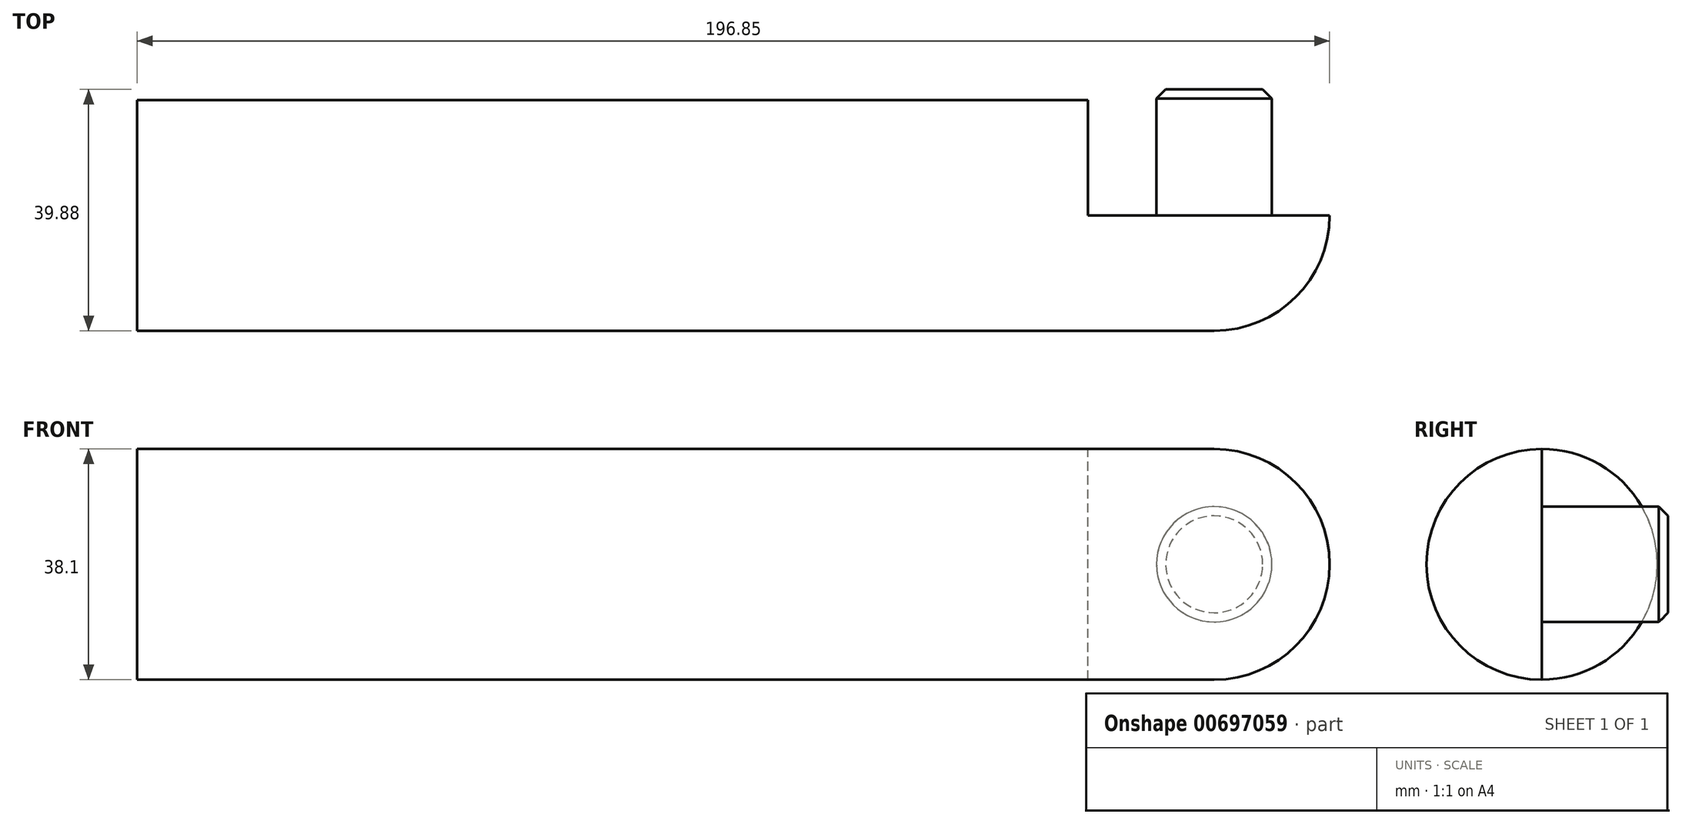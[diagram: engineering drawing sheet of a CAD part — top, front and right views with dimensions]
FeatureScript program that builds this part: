
annotation { "Feature Type Name" : "Feature", "Feature Type Description" : "" }
export const myFeature = defineFeature(function(context is Context, id is Id, definition is map)
    precondition{}
    {
        {
            var Q0;
            Q0=qCreatedBy(makeId("Front.planeOp"),FACE);
            var sketch = newSketch(context, id + "F0", { "sketchPlane" : qUnion([Q0])});
            skLineSegment(sketch, "E0.bottom", {"start": v(78.49, 19.05) * mm, "end": v(-78.49, 19.05) * mm});
            skLineSegment(sketch, "E0.top", {"start": v(78.49, -19.05) * mm, "end": v(-78.49, -19.05) * mm});
            skLineSegment(sketch, "E0.left", {"start": v(78.49, 19.05) * mm, "end": v(78.49, -19.05) * mm});
            skLineSegment(sketch, "E0.right", {"start": v(-78.49, 19.05) * mm, "end": v(-78.49, -19.05) * mm});
            skPoint(sketch, "E0.middle", {"position": v(0, 0) * mm});
            skLineSegment(sketch, "E1", {"start": v(78.49, 0) * mm, "end": v(-78.49, 0) * mm});
            skSolve(sketch);
        }
        {
            var Q0;
            Q0=qCreatedBy(makeId("Front.planeOp"),FACE);
            var sketch = newSketch(context, id + "F1", { "sketchPlane" : qUnion([Q0])});
            skLineSegment(sketch, "E2", {"start": v(78.49, 19.05) * mm, "end": v(99.31, 19.05) * mm});
            skLineSegment(sketch, "E3", {"start": v(78.49, -19.05) * mm, "end": v(99.31, -19.05) * mm});
            skLineSegment(sketch, "E4", {"start": v(99.31, 19.05) * mm, "end": v(99.31, -19.05) * mm});
            skLineSegment(sketch, "E5", {"start": v(78.49, 0) * mm, "end": v(99.31, 0) * mm});
            skLineSegment(sketch, "E6.0", {"start": v(78.49, 19.05) * mm, "end": v(78.49, -19.05) * mm});
            skSolve(sketch);
        }
        {
            var Q0;
            {var subQ0=sQuery(id+"F0.wireOp",EDGE,"E0.bottom");Q0=makeQuery(id+"F0.imprint","IMPRINT",FACE,{"disambiguationData":[TD([[makeQuery(id+"F0.imprint","IMPRINT",EDGE,{"derivedFrom":subQ0}),1.0]])]});}
            var Q1;
            Q1=sQuery(id+"F0.wireOp",EDGE,"E1");
            revolve(context, id + "F2", {"entities" : qUnion([Q0]), "axis" : qUnion([Q1]), "revolveType" : RevolveType.FULL});
        }
        {
            var Q0;
            {var subQ0=sQuery(id+"F1.wireOp",EDGE,"E2");Q0=makeQuery(id+"F1.imprint","IMPRINT",FACE,{"disambiguationData":[TD([[makeQuery(id+"F1.imprint","IMPRINT",EDGE,{"derivedFrom":subQ0}),-1.0]])]});}
            var Q1;
            Q1=sQuery(id+"F1.wireOp",EDGE,"E5");
            revolve(context, id + "F3", {"operationType" : NewBodyOperationType.ADD, "entities" : qUnion([Q0]), "axis" : qUnion([Q1]), "revolveType" : RevolveType.ONE_DIRECTION, "angle" : 180 * degree});
        }
        {
            var Q0;
            Q0=makeQuery(id+"F3.opRevolve","SWEPT_FACE",FACE,{"disambiguationData":[OSD([sQuery(id+"F1.wireOp",EDGE,"E4")])]});
            var Q1;
            Q1=sQuery(id+"F1.wireOp",EDGE,"E4");
            revolve(context, id + "F4", {"operationType" : NewBodyOperationType.ADD, "entities" : qUnion([Q0]), "axis" : qUnion([Q1]), "revolveType" : RevolveType.ONE_DIRECTION, "oppositeDirection" : true, "angle" : 90 * degree});
        }
        {
            var Q0;
            Q0=qCreatedBy(makeId("Front.planeOp"),FACE);
            var sketch = newSketch(context, id + "F5", { "sketchPlane" : qUnion([Q0])});
            skCircle(sketch, "E7", {"center": v(99.31, 0) * mm, "radius": 9.53 * mm});
            skSolve(sketch);
        }
        {
            var Q0;
            Q0=makeQuery(id+"F5.imprint","IMPRINT",FACE,{"disambiguationData":[TD([[makeQuery(id+"F5.imprint","IMPRINT",EDGE,{"derivedFrom":sQuery(id+"F5.wireOp",EDGE,"E7")}),1.0]])]});
            extrude(context, id + "F6", {"entities" : qUnion([Q0]), "operationType" : NewBodyOperationType.ADD, "oppositeDirection" : true, "depth" : 20.83 * mm});
        }
        {
            var Q0;
            Q0=makeQuery(id+"F6.opExtrude","CAP_FACE",FACE,{"disambiguationData":[OSD([sQuery(id+"F5.wireOp",EDGE,"E7")])],"isStart":false});
            chamfer(context, id + "F7", {"entities" : qUnion([Q0]), "chamferType" : ChamferType.OFFSET_ANGLE, "width" : 1.52 * mm, "oppositeDirection" : true, "angle" : 45 * degree, "tangentPropagation" : true});
        }
    });
